# Revit family: Evoflat 4.0F_RFA_2
name_source: partatom
category: Mechanical Equipment
units: mm (PartAtom-declared; Revit-internal decimal feet)

## family parameters
Always vertical = Yes
Classification = None
Cut with Voids When Loaded = No
OmniClass Number = 23.75.65.11.11
OmniClass Title = Heating Controllers
Part Type = Normal
Room Calculation Point = No
Round Connector Dimension = Use Diameter
Shared = No
Work Plane-Based = No

## types (8) — shared parameters
Connection = G 3/4 Internal Thread
D = 20 mm  [stored 0.0656168 ft]
Description = Flat Station
H = 613 mm  [stored 2.01115 ft]
H1 = 10 mm  [stored 0.0328084 ft]
H2 = 8 mm  [stored 0.0262467 ft]
H3 = 111 mm
Heating Capacity = 18 kW
Heating Circuit dT = 25 °C
Heating Flow Rate Supply = 600 l/h
Heating Total Pressure Loss Primary = 25 kPa
IfcExportAs = IfcFlowController
IfcExportType = EvoFlat 4.0 F
Insulation Material = Danfoss EPP insulation
L = 530 mm  [stored 1.73885 ft]
L1 = 96 mm  [stored 0.314961 ft]
L1a = 44 mm  [stored 0.144357 ft]
LOD 200 = No
LOD 350 = Yes
Manufacturer = Danfoss
Max Supply Temperature = 95 °C
Nominal Pressure = PN 10
Nut size = 30 mm
Type Image = <None>
URL = https://store.danfoss.com
Voltage = 230 V
W = 155 mm  [stored 0.50853 ft]
W1 = 44 mm  [stored 0.144357 ft]
Weight = 9.30 kg

## per-type parameters (varying)
| type | DHW Flow Rate Primary | DHW Pressure Loss Primary | DHW Tap Load 50°C | DHW Temperature DHS/DHR | DHW capacity | HEX material | Model | Model (Austria) | Model (France) | Model Type |
| Evoflat 4.0F_Type 1_Cu_183B1000 | 750 l/h | 32 kPa | 15.4 l/min | 65/16 °C | 43 kW | Danfoss Copper | 183B1000 | 183B1004 | 183B1008 | Evoflat 4.0F_Type 1_Cu |
| Evoflat 4.0F_Type 3_Cu_183B1002 | 943 l/h | 40 kPa | 19.8 l/min | 65/15 °C | 55 kW | Danfoss Copper | 183B1002 | 183B1006 | 183B1010 | Evoflat 4.0F_Type 3_Cu |
| Evoflat 4.0F_Type 2_Cu_183B1001 | 844 l/h | 35 kPa | 17.6 l/min | 65/15 °C | 49 kW | Danfoss Copper | 183B1001 | 183B1005 | 183B1009 | Evoflat 4.0F_Type 2_Cu |
| Evoflat 4.0F_Type 4_Cu_183B1003 | 1197 l/h | 57 kPa | 25.2 l/min | 65/14 °C | 70 kW | Danfoss Copper | 183B1003 | 183B1007 | 183B1011 | Evoflat 4.0F_Type 4_Cu |
| Evoflat 4.0F_Type 1_Sts_183B1500 | 750 l/h | 32 kPa | 15.4 l/min | 65/16 °C | 43 kW | Danfoss Stainless Steel | 183B1500 | 183B1504 | 183B1508 | Evoflat 4.0F_Type 1_Sts |
| Evoflat 4.0F_Type 2_Sts_183B1501 | 844 l/h | 35 kPa | 17.6 l/min | 65/15 °C | 49 kW | Danfoss Stainless Steel | 183B1501 | 183B1505 | 183B1509 | Evoflat 4.0F_Type 2_Sts |
| Evoflat 4.0F_Type 3_Sts_183B1502 | 943 l/h | 40 kPa | 19.8 l/min | 65/15 °C | 55 kW | Danfoss Stainless Steel | 183B1502 | 183B1506 | 183B1510 | Evoflat 4.0F_Type 3_Sts |
| Evoflat 4.0F_Type 4_Sts_183B1503 | 1197 l/h | 57 kPa | 25.2 l/min | 65/14 °C | 70 kW | Danfoss Stainless Steel | 183B1503 | 183B1507 | 183B1511 | Evoflat 4.0F_Type 4_Sts |

note: [stored X ft] marks values corroborated as IEEE doubles in the binary element streams (Revit-internal decimal feet)

## geometry (parser evidence)
native form markers: Sweep x1
no freeform markers — native parametric forms only
